FCSTD DOCUMENT  (FreeCAD 1.0R39109 (Git))
Label: PrintBedSize
License: All rights reserved
LicenseURL: http://en.wikipedia.org/wiki/All_rights_reserved
objects: Sketcher::SketchObject×1, PartDesign::Body×1, App::Part×1
note: 3 computed .brp shape members not serialized (recipe doc carries the construction recipe); baked Part::Feature solids carry a one-line shape summary decoded from their .brp

FEATURE [Sketcher::SketchObject] Sketch
  ArcFitTolerance = 1e-06
  AttachmentSupport = -> [XY_Plane]
  FullyConstrained = true
  MakeInternals = false
  MapMode = 5
  sketch-geometry (4):
    g0: LineSegment StartX=-125 StartY=125 StartZ=0 EndX=-125 EndY=-125 EndZ=0
    g1: LineSegment StartX=-125 StartY=-125 StartZ=0 EndX=125 EndY=-125 EndZ=0
    g2: LineSegment StartX=125 StartY=-125 StartZ=0 EndX=125 EndY=125 EndZ=0
    g3: LineSegment StartX=125 StartY=125 StartZ=0 EndX=-125 EndY=125 EndZ=0
  constraints (11):
    c: Coincident(g0,g1)
    c: Coincident(g1,g2)
    c: Coincident(g2,g3)
    c: Coincident(g3,g0)
    c: Vertical(g0)
    c: Vertical(g2)
    c: Horizontal(g1)
    c: Horizontal(g3)
    c: Symmetric(g2,g0,g-1)
    c: DistanceY(g2,g2) = 250
    c: Equal(g2,g3)
FEATURE [PartDesign::Body] Body
  AllowCompound = false
  Group = -> [Sketch]
  Origin = -> Origin
FEATURE [App::Part] Part  label="PrintBedSize"
  Group = -> [Body]
  Origin = -> Origin001
